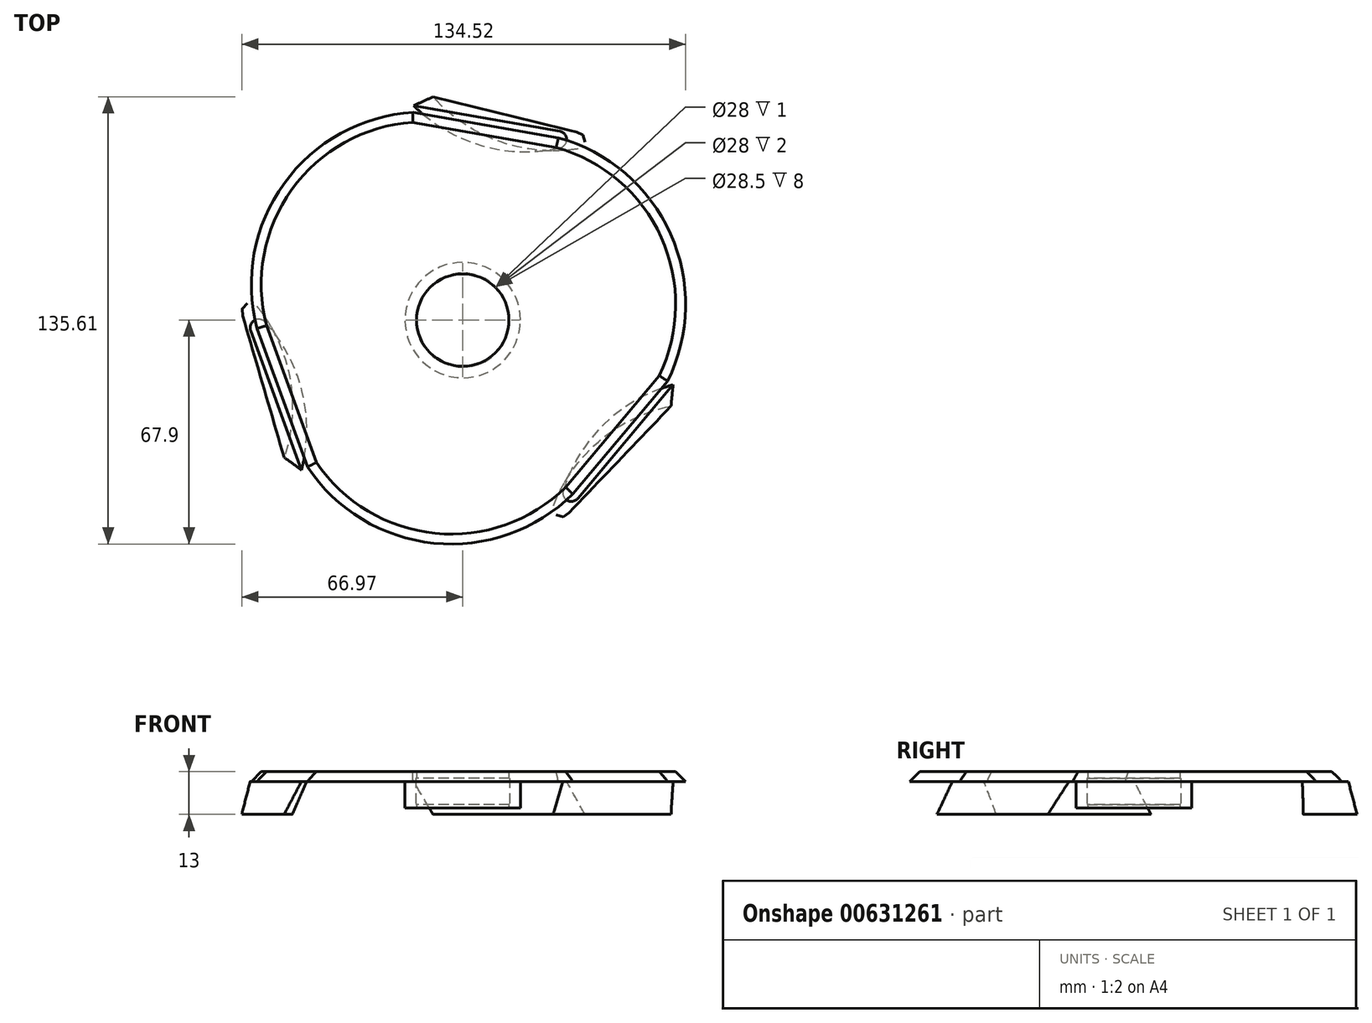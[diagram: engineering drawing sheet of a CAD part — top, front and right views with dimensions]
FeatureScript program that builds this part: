
annotation { "Feature Type Name" : "Feature", "Feature Type Description" : "" }
export const myFeature = defineFeature(function(context is Context, id is Id, definition is map)
    precondition{}
    {
        {
            var Q0;
            Q0=qCreatedBy(makeId("Top.planeOp"),FACE);
            var sketch = newSketch(context, id + "F0", { "sketchPlane" : qUnion([Q0])});
            skLineSegment(sketch, "E0", {"start": v(61.47, 25.98) * mm, "end": v(61.47, -19.02) * mm});
            skArc(sketch, "E1", {"start": v(56.57, -20) * mm, "mid": v(59.42, -21.52) * mm, "end": v(61.47, -19.02) * mm});
            skArc(sketch, "E2", {"start": v(56.57, -20) * mm, "mid": v(53.14, 3.62) * mm, "end": v(61.47, 25.98) * mm});
            skSolve(sketch);
        }
        {
            var Q0;
            Q0=qCreatedBy(makeId("Top.planeOp"),FACE);
            cPlane(context, id + "F1", {"entities" : qUnion([Q0]), "cplaneType" : CPlaneType.OFFSET, "offset" : 25 * mm, "width" : 150 * mm, "height" : 150 * mm});
        }
        {
            var Q0;
            Q0=qCreatedBy(id+"F1.planeOp",FACE);
            var sketch = newSketch(context, id + "F2", { "sketchPlane" : qUnion([Q0])});
            skLineSegment(sketch, "E3", {"start": v(61.53, 37.23) * mm, "end": v(70.22, -12) * mm});
            skArc(sketch, "E4", {"start": v(65.56, -13.83) * mm, "mid": v(68.63, -14.83) * mm, "end": v(70.22, -12) * mm});
            skArc(sketch, "E5", {"start": v(65.56, -13.83) * mm, "mid": v(57.15, 11.2) * mm, "end": v(61.53, 37.23) * mm});
            skLineSegment(sketch, "E6", {"start": v(0, 0) * mm, "end": v(59.09, 10.42) * mm});
            skSolve(sketch);
        }
        {
            var Q0;
            Q0=qCreatedBy(id+"F1.planeOp",FACE);
            cPlane(context, id + "F3", {"entities" : qUnion([Q0]), "cplaneType" : CPlaneType.OFFSET, "offset" : 25 * mm, "width" : 150 * mm, "height" : 150 * mm});
        }
        {
            var Q0;
            Q0=qCreatedBy(id+"F3.planeOp",FACE);
            var sketch = newSketch(context, id + "F4", { "sketchPlane" : qUnion([Q0])});
            skLineSegment(sketch, "E7", {"start": v(60.41, 51.76) * mm, "end": v(80.93, -4.62) * mm});
            skArc(sketch, "E8", {"start": v(76.66, -7.22) * mm, "mid": v(79.86, -7.67) * mm, "end": v(80.93, -4.62) * mm});
            skArc(sketch, "E9", {"start": v(76.66, -7.22) * mm, "mid": v(61.4, 20.3) * mm, "end": v(60.41, 51.76) * mm});
            skLineSegment(sketch, "E10", {"start": v(0, 0) * mm, "end": v(56.38, 20.52) * mm});
            skSolve(sketch);
        }
        {
            var Q0;
            Q0=qCreatedBy(id+"F3.planeOp",FACE);
            cPlane(context, id + "F5", {"entities" : qUnion([Q0]), "cplaneType" : CPlaneType.OFFSET, "offset" : 25 * mm, "width" : 150 * mm, "height" : 150 * mm});
        }
        {
            var Q0;
            Q0=qCreatedBy(id+"F5.planeOp",FACE);
            var sketch = newSketch(context, id + "F6", { "sketchPlane" : qUnion([Q0])});
            skLineSegment(sketch, "E11", {"start": v(46.2, 79.77) * mm, "end": v(88.7, 6.16) * mm});
            skArc(sketch, "E12", {"start": v(84.95, 2.86) * mm, "mid": v(88.18, 2.97) * mm, "end": v(88.7, 6.16) * mm});
            skArc(sketch, "E13", {"start": v(84.95, 2.86) * mm, "mid": v(56.74, 36.86) * mm, "end": v(46.2, 79.77) * mm});
            skLineSegment(sketch, "E14", {"start": v(0, 0) * mm, "end": v(51.96, 30) * mm});
            skSolve(sketch);
        }
        {
            var Q0;
            Q0=qCreatedBy(id+"F5.planeOp",FACE);
            cPlane(context, id + "F7", {"entities" : qUnion([Q0]), "cplaneType" : CPlaneType.OFFSET, "offset" : 25 * mm, "width" : 150 * mm, "height" : 150 * mm});
        }
        {
            var Q0;
            Q0=qCreatedBy(id+"F7.planeOp",FACE);
            var sketch = newSketch(context, id + "F8", { "sketchPlane" : qUnion([Q0])});
            skLineSegment(sketch, "E15", {"start": v(34.74, 82.65) * mm, "end": v(92.6, 13.7) * mm});
            skArc(sketch, "E16", {"start": v(89.46, 9.8) * mm, "mid": v(92.63, 10.47) * mm, "end": v(92.6, 13.7) * mm});
            skArc(sketch, "E17", {"start": v(89.46, 9.8) * mm, "mid": v(53.8, 39.98) * mm, "end": v(34.74, 82.65) * mm});
            skLineSegment(sketch, "E18", {"start": v(0, 0) * mm, "end": v(45.96, 38.57) * mm});
            skSolve(sketch);
        }
        {
            var Q0;
            Q0=qCreatedBy(id+"F7.planeOp",FACE);
            cPlane(context, id + "F9", {"entities" : qUnion([Q0]), "cplaneType" : CPlaneType.OFFSET, "offset" : 25 * mm, "width" : 150 * mm, "height" : 150 * mm});
        }
        {
            var Q0;
            Q0=qCreatedBy(id+"F9.planeOp",FACE);
            var sketch = newSketch(context, id + "F10", { "sketchPlane" : qUnion([Q0])});
            skLineSegment(sketch, "E19", {"start": v(18.11, 85.34) * mm, "end": v(83.22, 30.7) * mm});
            skArc(sketch, "E20", {"start": v(80.82, 26.31) * mm, "mid": v(83.82, 27.52) * mm, "end": v(83.22, 30.7) * mm});
            skArc(sketch, "E21", {"start": v(80.82, 26.31) * mm, "mid": v(42.69, 48.62) * mm, "end": v(18.11, 85.34) * mm});
            skLineSegment(sketch, "E22", {"start": v(0, 0) * mm, "end": v(38.57, 45.96) * mm});
            skSolve(sketch);
        }
        {
            var Q0;
            Q0=qCreatedBy(id+"F9.planeOp",FACE);
            cPlane(context, id + "F11", {"entities" : qUnion([Q0]), "cplaneType" : CPlaneType.OFFSET, "offset" : 25 * mm, "width" : 150 * mm, "height" : 150 * mm});
        }
        {
            var Q0;
            Q0=qCreatedBy(id+"F11.planeOp",FACE);
            var sketch = newSketch(context, id + "F12", { "sketchPlane" : qUnion([Q0])});
            skLineSegment(sketch, "E23", {"start": v(6.79, 79.72) * mm, "end": v(67.4, 44.72) * mm});
            skArc(sketch, "E24", {"start": v(65.8, 39.98) * mm, "mid": v(68.55, 41.7) * mm, "end": v(67.4, 44.72) * mm});
            skArc(sketch, "E25", {"start": v(65.8, 39.98) * mm, "mid": v(31.6, 52.88) * mm, "end": v(6.79, 79.72) * mm});
            skLineSegment(sketch, "E26", {"start": v(0, 0) * mm, "end": v(30, 51.96) * mm});
            skSolve(sketch);
        }
        {
            var Q0;
            Q0=qCreatedBy(id+"F11.planeOp",FACE);
            cPlane(context, id + "F13", {"entities" : qUnion([Q0]), "cplaneType" : CPlaneType.OFFSET, "offset" : 25 * mm, "width" : 150 * mm, "height" : 150 * mm});
        }
        {
            var Q0;
            Q0=qCreatedBy(id+"F13.planeOp",FACE);
            var sketch = newSketch(context, id + "F14", { "sketchPlane" : qUnion([Q0])});
            skLineSegment(sketch, "E27", {"start": v(-1.48, 71.9) * mm, "end": v(45.5, 54.8) * mm});
            skArc(sketch, "E28", {"start": v(44.75, 49.86) * mm, "mid": v(47.16, 52.02) * mm, "end": v(45.5, 54.8) * mm});
            skArc(sketch, "E29", {"start": v(44.75, 49.86) * mm, "mid": v(18.88, 55.1) * mm, "end": v(-1.48, 71.9) * mm});
            skLineSegment(sketch, "E30", {"start": v(0, 0) * mm, "end": v(20.52, 56.38) * mm});
            skSolve(sketch);
        }
        {
            var Q0;
            Q0=qCreatedBy(id+"F13.planeOp",FACE);
            cPlane(context, id + "F15", {"entities" : qUnion([Q0]), "cplaneType" : CPlaneType.OFFSET, "offset" : 25 * mm, "width" : 150 * mm, "height" : 150 * mm});
        }
        {
            var Q0;
            Q0=qCreatedBy(id+"F15.planeOp",FACE);
            var sketch = newSketch(context, id + "F16", { "sketchPlane" : qUnion([Q0])});
            skLineSegment(sketch, "E31", {"start": v(-14.91, 65.05) * mm, "end": v(29.4, 57.23) * mm});
            skArc(sketch, "E32", {"start": v(29.52, 52.24) * mm, "mid": v(31.51, 54.78) * mm, "end": v(29.4, 57.23) * mm});
            skArc(sketch, "E33", {"start": v(29.52, 52.24) * mm, "mid": v(5.66, 52.96) * mm, "end": v(-14.91, 65.05) * mm});
            skLineSegment(sketch, "E34", {"start": v(0, 0) * mm, "end": v(10.42, 59.09) * mm});
            skSolve(sketch);
        }
        {
            var Q0;
            Q0=qCreatedBy(makeId("Front.planeOp"),FACE);
            var sketch = newSketch(context, id + "F17", { "sketchPlane" : qUnion([Q0])});
            skLineSegment(sketch, "E35.bottom", {"start": v(0, -53.56) * mm, "end": v(114.22, -53.56) * mm});
            skLineSegment(sketch, "E35.top", {"start": v(0, 159.78) * mm, "end": v(114.22, 159.78) * mm});
            skLineSegment(sketch, "E35.left", {"start": v(0, -53.56) * mm, "end": v(0, 159.78) * mm});
            skLineSegment(sketch, "E35.right", {"start": v(114.22, -53.56) * mm, "end": v(114.22, 159.78) * mm});
            skSolve(sketch);
        }
        {
            var Q0;
            Q0=makeQuery(id+"F0.imprint","IMPRINT",FACE,{"disambiguationData":[TD([[makeQuery(id+"F0.imprint","IMPRINT",EDGE,{"derivedFrom":sQuery(id+"F0.wireOp",EDGE,"E0")}),-1.0]])]});
            var Q1;
            {var subQ0=sQuery(id+"F2.wireOp",EDGE,"E3");Q1=makeQuery(id+"F2.imprint","IMPRINT",FACE,{"disambiguationData":[TD([[makeQuery(id+"F2.imprint","IMPRINT",EDGE,{"derivedFrom":subQ0}),-1.0]])]});}
            var Q2;
            Q2=makeQuery(id+"F4.imprint","IMPRINT",FACE,{"disambiguationData":[TD([[makeQuery(id+"F4.imprint","IMPRINT",EDGE,{"derivedFrom":sQuery(id+"F4.wireOp",EDGE,"E7")}),-1.0]])]});
            var Q3;
            Q3=makeQuery(id+"F6.imprint","IMPRINT",FACE,{"disambiguationData":[TD([[makeQuery(id+"F6.imprint","IMPRINT",EDGE,{"derivedFrom":sQuery(id+"F6.wireOp",EDGE,"E11")}),-1.0]])]});
            var Q4;
            Q4=makeQuery(id+"F8.imprint","IMPRINT",FACE,{"disambiguationData":[TD([[makeQuery(id+"F8.imprint","IMPRINT",EDGE,{"derivedFrom":sQuery(id+"F8.wireOp",EDGE,"E15")}),-1.0]])]});
            var Q5;
            Q5=makeQuery(id+"F10.imprint","IMPRINT",FACE,{"disambiguationData":[TD([[makeQuery(id+"F10.imprint","IMPRINT",EDGE,{"derivedFrom":sQuery(id+"F10.wireOp",EDGE,"E19")}),-1.0]])]});
            var Q6;
            Q6=makeQuery(id+"F12.imprint","IMPRINT",FACE,{"disambiguationData":[TD([[makeQuery(id+"F12.imprint","IMPRINT",EDGE,{"derivedFrom":sQuery(id+"F12.wireOp",EDGE,"E23")}),-1.0]])]});
            var Q7;
            {var subQ0=sQuery(id+"F14.wireOp",EDGE,"E27");Q7=makeQuery(id+"F14.imprint","IMPRINT",FACE,{"disambiguationData":[TD([[makeQuery(id+"F14.imprint","IMPRINT",EDGE,{"derivedFrom":subQ0}),-1.0]])]});}
            var Q8;
            {var subQ0=sQuery(id+"F16.wireOp",EDGE,"E31");Q8=makeQuery(id+"F16.imprint","IMPRINT",FACE,{"disambiguationData":[TD([[makeQuery(id+"F16.imprint","IMPRINT",EDGE,{"derivedFrom":subQ0}),-1.0]])]});}
            loft(context, id + "F18", {"sheetProfilesArray" : [{ "sheetProfileEntities" : qUnion([Q0]) }, { "sheetProfileEntities" : qUnion([Q1]) }, { "sheetProfileEntities" : qUnion([Q2]) }, { "sheetProfileEntities" : qUnion([Q3]) }, { "sheetProfileEntities" : qUnion([Q4]) }, { "sheetProfileEntities" : qUnion([Q5]) }, { "sheetProfileEntities" : qUnion([Q6]) }, { "sheetProfileEntities" : qUnion([Q7]) }, { "sheetProfileEntities" : qUnion([Q8]) }]});
        }
        {
            var Q0;
            {var subQ0=sQuery(id+"F16.wireOp",EDGE,"E31");Q0=makeQuery(id+"F18.opLoft","SWEPT_BODY",BODY,{"disambiguationData":[OSD([makeQuery(id+"F0.imprint","IMPRINT",FACE,{"disambiguationData":[TD([[makeQuery(id+"F0.imprint","IMPRINT",EDGE,{"derivedFrom":sQuery(id+"F0.wireOp",EDGE,"E0")}),-1.0]])]}),sQuery(id+"F2.wireOp",EDGE,"E5"),sQuery(id+"F4.wireOp",EDGE,"E9"),sQuery(id+"F6.wireOp",EDGE,"E13"),sQuery(id+"F8.wireOp",EDGE,"E17"),sQuery(id+"F10.wireOp",EDGE,"E21"),sQuery(id+"F12.wireOp",EDGE,"E25"),sQuery(id+"F14.wireOp",EDGE,"E29"),makeQuery(id+"F16.imprint","IMPRINT",FACE,{"disambiguationData":[TD([[makeQuery(id+"F16.imprint","IMPRINT",EDGE,{"derivedFrom":subQ0}),-1.0]])]})])]});}
            var Q1;
            Q1=sQuery(id+"F17.wireOp",EDGE,"E35.left");
            circularPattern(context, id + "F19", {"entities" : qUnion([Q0]), "axis" : qUnion([Q1]), "angle" : 360 * degree, "instanceCount" : 3, "equalSpace" : true});
        }
        {
            var Q0;
            Q0=qCreatedBy(makeId("Top.planeOp"),FACE);
            var sketch = newSketch(context, id + "F20", { "sketchPlane" : qUnion([Q0])});
            skArc(sketch, "E36", {"start": v(-20, 0) * mm, "mid": v(15, -35) * mm, "end": v(50, 0) * mm});
            skArc(sketch, "E37.0", {"start": v(-23, 0) * mm, "mid": v(15, -38) * mm, "end": v(53, 0) * mm});
            skLineSegment(sketch, "E38", {"start": v(-23, 0) * mm, "end": v(-20, 0) * mm});
            skLineSegment(sketch, "E39", {"start": v(50, 0) * mm, "end": v(53, 0) * mm});
            skSolve(sketch);
        }
        {
            var Q0;
            Q0 = qSketchRegion(id + "F20", true);
            var Q1;
            Q1=makeQuery(id+"F20.imprint","IMPRINT",FACE,{"disambiguationData":[TD([[makeQuery(id+"F20.imprint","IMPRINT",EDGE,{"derivedFrom":sQuery(id+"F20.wireOp",EDGE,"E36")}),-1.0]])]});
            extrude(context, id + "F21", {"entities" : qUnion([Q0, Q1]), "depth" : 125 * mm, "offsetDistance" : 25 * mm, "hasSecondDirection" : true, "secondDirectionOppositeDirection" : false, "secondDirectionDepth" : 75 * mm});
        }
        {
            var Q0;
            Q0=makeQuery(id+"F21.opExtrude","SWEPT_BODY",BODY,{"disambiguationData":[OSD([sQuery(id+"F20.wireOp",EDGE,"E36"),sQuery(id+"F20.wireOp",EDGE,"E37.0"),sQuery(id+"F20.wireOp",EDGE,"E38"),sQuery(id+"F20.wireOp",EDGE,"E39")])]});
            var Q1;
            Q1=sQuery(id+"F17.wireOp",EDGE,"E35.left");
            circularPattern(context, id + "F22", {"entities" : qUnion([Q0]), "axis" : qUnion([Q1]), "angle" : 360 * degree, "instanceCount" : 3, "equalSpace" : true});
        }
        {
            var Q0;
            Q0=qCreatedBy(makeId("Front.planeOp"),FACE);
            cPlane(context, id + "F23", {"entities" : qUnion([Q0]), "cplaneType" : CPlaneType.OFFSET, "offset" : 40 * mm, "width" : 150 * mm, "height" : 150 * mm});
        }
        {
            var Q0;
            Q0=qCreatedBy(id+"F23.planeOp",FACE);
            var sketch = newSketch(context, id + "F24", { "sketchPlane" : qUnion([Q0])});
            skEllipse(sketch, "E40", {"center": v(11.35, 100.28) * mm, "majorRadius": 20.63 * mm, "minorRadius": 3.95 * mm, "majorAxis": v(-1, 0)});
            skSolve(sketch);
        }
        {
            var Q0;
            Q0 = qSketchRegion(id + "F24", true);
            var Q1;
            Q1=makeQuery(id+"F21.opExtrude","SWEPT_BODY",BODY,{"disambiguationData":[OSD([sQuery(id+"F20.wireOp",EDGE,"E36"),sQuery(id+"F20.wireOp",EDGE,"E37.0"),sQuery(id+"F20.wireOp",EDGE,"E38"),sQuery(id+"F20.wireOp",EDGE,"E39")])]});
            var Q2;
            {var subQ0=sQuery(id+"F16.wireOp",EDGE,"E31");Q2=makeQuery(id+"F19.opPattern","COPY",BODY,{"derivedFrom":makeQuery(id+"F18.opLoft","SWEPT_BODY",BODY,{"disambiguationData":[OSD([makeQuery(id+"F0.imprint","IMPRINT",FACE,{"disambiguationData":[TD([[makeQuery(id+"F0.imprint","IMPRINT",EDGE,{"derivedFrom":sQuery(id+"F0.wireOp",EDGE,"E0")}),-1.0]])]}),sQuery(id+"F2.wireOp",EDGE,"E5"),sQuery(id+"F4.wireOp",EDGE,"E9"),sQuery(id+"F6.wireOp",EDGE,"E13"),sQuery(id+"F8.wireOp",EDGE,"E17"),sQuery(id+"F10.wireOp",EDGE,"E21"),sQuery(id+"F12.wireOp",EDGE,"E25"),sQuery(id+"F14.wireOp",EDGE,"E29"),makeQuery(id+"F16.imprint","IMPRINT",FACE,{"disambiguationData":[TD([[makeQuery(id+"F16.imprint","IMPRINT",EDGE,{"derivedFrom":subQ0}),-1.0]])]})])]}),"instanceName":"2"});}
            extrude(context, id + "F25", {"entities" : qUnion([Q0]), "endBound" : BoundingType.UP_TO_BODY, "oppositeDirection" : true, "depth" : 25 * mm, "endBoundEntityBody" : qUnion([Q1]), "offsetDistance" : 25 * mm, "hasSecondDirection" : true, "secondDirectionBound" : SecondDirectionBoundingType.UP_TO_BODY, "secondDirectionOppositeDirection" : false, "secondDirectionDepth" : 25 * mm, "secondDirectionBoundEntityBody" : qUnion([Q2])});
        }
        {
            var Q0;
            Q0=makeQuery(id+"F25.opExtrude","SWEPT_BODY",BODY,{"disambiguationData":[OSD([sQuery(id+"F24.wireOp",EDGE,"E40")])]});
            var Q1;
            Q1=sQuery(id+"F17.wireOp",EDGE,"E35.left");
            circularPattern(context, id + "F26", {"entities" : qUnion([Q0]), "axis" : qUnion([Q1]), "angle" : 360 * degree, "instanceCount" : 3, "equalSpace" : true});
        }
        {
            var Q0;
            Q0=qCreatedBy(id+"F15.planeOp",FACE);
            var sketch = newSketch(context, id + "F27", { "sketchPlane" : qUnion([Q0])});
            skArc(sketch, "E41", {"start": v(63.79, -19.6) * mm, "mid": v(64.81, 26.96) * mm, "end": v(29.42, 57.23) * mm});
            skArc(sketch, "E42.1.0", {"start": v(-14.92, 65.04) * mm, "mid": v(-55.76, 42.65) * mm, "end": v(-64.27, -3.14) * mm});
            skArc(sketch, "E42.2.0", {"start": v(-48.87, -45.44) * mm, "mid": v(-9.06, -69.6) * mm, "end": v(34.86, -54.1) * mm});
            skPoint(sketch, "E42.center", {"position": v(0, 0) * mm});
            skLineSegment(sketch, "E43", {"start": v(-14.92, 65.04) * mm, "end": v(29.42, 57.23) * mm});
            skLineSegment(sketch, "E44", {"start": v(63.79, -19.6) * mm, "end": v(34.86, -54.1) * mm});
            skLineSegment(sketch, "E45", {"start": v(-48.87, -45.44) * mm, "end": v(-64.27, -3.14) * mm});
            skSolve(sketch);
        }
        {
            var Q0;
            Q0 = qSketchRegion(id + "F27", true);
            extrude(context, id + "F28", {"entities" : qUnion([Q0]), "depth" : 3 * mm, "offsetDistance" : 25 * mm});
        }
        {
            var Q0;
            Q0=qCreatedBy(makeId("Top.planeOp"),FACE);
            var sketch = newSketch(context, id + "F29", { "sketchPlane" : qUnion([Q0])});
            skArc(sketch, "E46", {"start": v(61.47, 25.98) * mm, "mid": v(33.46, 64.35) * mm, "end": v(-14.02, 62.86) * mm});
            skArc(sketch, "E47.1.0", {"start": v(-53.24, 40.25) * mm, "mid": v(-72.46, -3.2) * mm, "end": v(-47.43, -43.57) * mm});
            skArc(sketch, "E47.2.0", {"start": v(-8.24, -66.23) * mm, "mid": v(39, -61.15) * mm, "end": v(61.44, -19.3) * mm});
            skPoint(sketch, "E47.center", {"position": v(0, 0) * mm});
            skLineSegment(sketch, "E48", {"start": v(61.44, -19.3) * mm, "end": v(61.47, 25.98) * mm});
            skLineSegment(sketch, "E49", {"start": v(-8.24, -66.23) * mm, "end": v(-47.43, -43.57) * mm});
            skLineSegment(sketch, "E50", {"start": v(-53.24, 40.25) * mm, "end": v(-14.02, 62.86) * mm});
            skSolve(sketch);
        }
        {
            var Q0;
            Q0 = qSketchRegion(id + "F29", true);
            extrude(context, id + "F30", {"entities" : qUnion([Q0]), "oppositeDirection" : true, "depth" : 3 * mm, "offsetDistance" : 25 * mm});
        }
        {
            var Q0;
            Q0=qCreatedBy(makeId("Top.planeOp"),FACE);
            var sketch = newSketch(context, id + "F31", { "sketchPlane" : qUnion([Q0])});
            skCircle(sketch, "E51", {"center": v(0, 0) * mm, "radius": 17.5 * mm});
            skSolve(sketch);
        }
        {
            var Q0;
            Q0 = qSketchRegion(id + "F31", true);
            extrude(context, id + "F32", {"entities" : qUnion([Q0]), "operationType" : NewBodyOperationType.ADD, "depth" : 8 * mm, "offsetDistance" : 25 * mm});
        }
        {
            var Q0;
            Q0=qCreatedBy(makeId("Top.planeOp"),FACE);
            var sketch = newSketch(context, id + "F33", { "sketchPlane" : qUnion([Q0])});
            skCircle(sketch, "E52", {"center": v(0, 0) * mm, "radius": 14 * mm});
            skSolve(sketch);
        }
        {
            var Q0;
            Q0 = qSketchRegion(id + "F33", true);
            extrude(context, id + "F34", {"entities" : qUnion([Q0]), "operationType" : NewBodyOperationType.REMOVE, "oppositeDirection" : true, "depth" : 25 * mm, "offsetDistance" : 25 * mm, "hasSecondDirection" : true, "secondDirectionOppositeDirection" : false, "secondDirectionDepth" : 25 * mm});
        }
        {
            var Q0;
            Q0=qCreatedBy(makeId("Top.planeOp"),FACE);
            var sketch = newSketch(context, id + "F35", { "sketchPlane" : qUnion([Q0])});
            skCircle(sketch, "E53", {"center": v(0, 0) * mm, "radius": 14.25 * mm});
            skSolve(sketch);
        }
        {
            var Q0;
            Q0 = qSketchRegion(id + "F35", true);
            extrude(context, id + "F36", {"entities" : qUnion([Q0]), "operationType" : NewBodyOperationType.REMOVE, "depth" : 6 * mm, "offsetDistance" : 25 * mm, "hasSecondDirection" : true, "secondDirectionOppositeDirection" : true, "secondDirectionDepth" : 2 * mm});
        }
        {
            var Q0;
            Q0=qCreatedBy(id+"F15.planeOp",FACE);
            var sketch = newSketch(context, id + "F37", { "sketchPlane" : qUnion([Q0])});
            skCircle(sketch, "E54", {"center": v(0, 0) * mm, "radius": 17.5 * mm});
            skSolve(sketch);
        }
        {
            var Q0;
            Q0 = qSketchRegion(id + "F37", true);
            extrude(context, id + "F38", {"entities" : qUnion([Q0]), "operationType" : NewBodyOperationType.ADD, "oppositeDirection" : true, "depth" : 8 * mm, "offsetDistance" : 25 * mm});
        }
        {
            var Q0;
            Q0=qCreatedBy(id+"F15.planeOp",FACE);
            var sketch = newSketch(context, id + "F39", { "sketchPlane" : qUnion([Q0])});
            skCircle(sketch, "E55", {"center": v(0, 0) * mm, "radius": 14 * mm});
            skSolve(sketch);
        }
        {
            var Q0;
            Q0 = qSketchRegion(id + "F39", true);
            extrude(context, id + "F40", {"entities" : qUnion([Q0]), "operationType" : NewBodyOperationType.REMOVE, "depth" : 25 * mm, "offsetDistance" : 25 * mm, "hasSecondDirection" : true, "secondDirectionOppositeDirection" : true, "secondDirectionDepth" : 25 * mm});
        }
        {
            var Q0;
            Q0=qCreatedBy(id+"F15.planeOp",FACE);
            var sketch = newSketch(context, id + "F41", { "sketchPlane" : qUnion([Q0])});
            skCircle(sketch, "E56", {"center": v(0, 0) * mm, "radius": 14.25 * mm});
            skSolve(sketch);
        }
        {
            var Q0;
            Q0 = qSketchRegion(id + "F41", true);
            extrude(context, id + "F42", {"entities" : qUnion([Q0]), "operationType" : NewBodyOperationType.REMOVE, "depth" : 1 * mm, "offsetDistance" : 25 * mm, "hasSecondDirection" : true, "secondDirectionOppositeDirection" : true, "secondDirectionDepth" : 7 * mm});
        }
        {
            var Q0;
            Q0=makeQuery(id+"F28.opExtrude","CAP_EDGE",EDGE,{"disambiguationData":[OSD([sQuery(id+"F27.wireOp",EDGE,"E42.2.0")])],"isStart":false});
            var Q1;
            Q1=makeQuery(id+"F28.opExtrude","CAP_EDGE",EDGE,{"disambiguationData":[OSD([sQuery(id+"F27.wireOp",EDGE,"E44")])],"isStart":false});
            var Q2;
            Q2=makeQuery(id+"F28.opExtrude","CAP_EDGE",EDGE,{"disambiguationData":[OSD([sQuery(id+"F27.wireOp",EDGE,"E41")])],"isStart":false});
            var Q3;
            Q3=makeQuery(id+"F28.opExtrude","CAP_EDGE",EDGE,{"disambiguationData":[OSD([sQuery(id+"F27.wireOp",EDGE,"E45")])],"isStart":false});
            var Q4;
            Q4=makeQuery(id+"F28.opExtrude","CAP_EDGE",EDGE,{"disambiguationData":[OSD([sQuery(id+"F27.wireOp",EDGE,"E42.1.0")])],"isStart":false});
            var Q5;
            Q5=makeQuery(id+"F28.opExtrude","CAP_EDGE",EDGE,{"disambiguationData":[OSD([sQuery(id+"F27.wireOp",EDGE,"E43")])],"isStart":false});
            chamfer(context, id + "F43", {"entities" : qUnion([Q0, Q1, Q2, Q3, Q4, Q5]), "width" : 5 * mm, "tangentPropagation" : true});
        }
        {
            var Q0;
            Q0=makeQuery(id+"F30.opExtrude","CAP_EDGE",EDGE,{"disambiguationData":[OSD([sQuery(id+"F29.wireOp",EDGE,"E46")])],"isStart":false});
            var Q1;
            Q1=makeQuery(id+"F30.opExtrude","CAP_EDGE",EDGE,{"disambiguationData":[OSD([sQuery(id+"F29.wireOp",EDGE,"E50")])],"isStart":false});
            var Q2;
            Q2=makeQuery(id+"F30.opExtrude","CAP_EDGE",EDGE,{"disambiguationData":[OSD([sQuery(id+"F29.wireOp",EDGE,"E47.1.0")])],"isStart":false});
            var Q3;
            Q3=makeQuery(id+"F30.opExtrude","CAP_EDGE",EDGE,{"disambiguationData":[OSD([sQuery(id+"F29.wireOp",EDGE,"E49")])],"isStart":false});
            var Q4;
            Q4=makeQuery(id+"F30.opExtrude","CAP_EDGE",EDGE,{"disambiguationData":[OSD([sQuery(id+"F29.wireOp",EDGE,"E47.2.0")])],"isStart":false});
            var Q5;
            Q5=makeQuery(id+"F30.opExtrude","CAP_EDGE",EDGE,{"disambiguationData":[OSD([sQuery(id+"F29.wireOp",EDGE,"E48")])],"isStart":false});
            chamfer(context, id + "F44", {"entities" : qUnion([Q0, Q1, Q2, Q3, Q4, Q5]), "width" : 5 * mm, "tangentPropagation" : true});
        }
        {
            var Q0;
            Q0=qCreatedBy(makeId("Right.planeOp"),FACE);
            var sketch = newSketch(context, id + "F45", { "sketchPlane" : qUnion([Q0])});
            skLineSegment(sketch, "E57.bottom", {"start": v(90, 190) * mm, "end": v(-90, 190) * mm});
            skLineSegment(sketch, "E57.top", {"start": v(90, -10) * mm, "end": v(-90, -10) * mm});
            skLineSegment(sketch, "E57.left", {"start": v(90, 190) * mm, "end": v(90, -10) * mm});
            skLineSegment(sketch, "E57.right", {"start": v(-90, 190) * mm, "end": v(-90, -10) * mm});
            skSolve(sketch);
        }
        {
            var Q0;
            Q0 = qSketchRegion(id + "F45", true);
            extrude(context, id + "F46", {"entities" : qUnion([Q0]), "operationType" : NewBodyOperationType.REMOVE, "endBound" : BoundingType.THROUGH_ALL, "oppositeDirection" : true, "depth" : 25 * mm, "offsetDistance" : 25 * mm, "hasSecondDirection" : true, "secondDirectionBound" : SecondDirectionBoundingType.THROUGH_ALL, "secondDirectionOppositeDirection" : false, "secondDirectionDepth" : 25 * mm});
        }
    });
